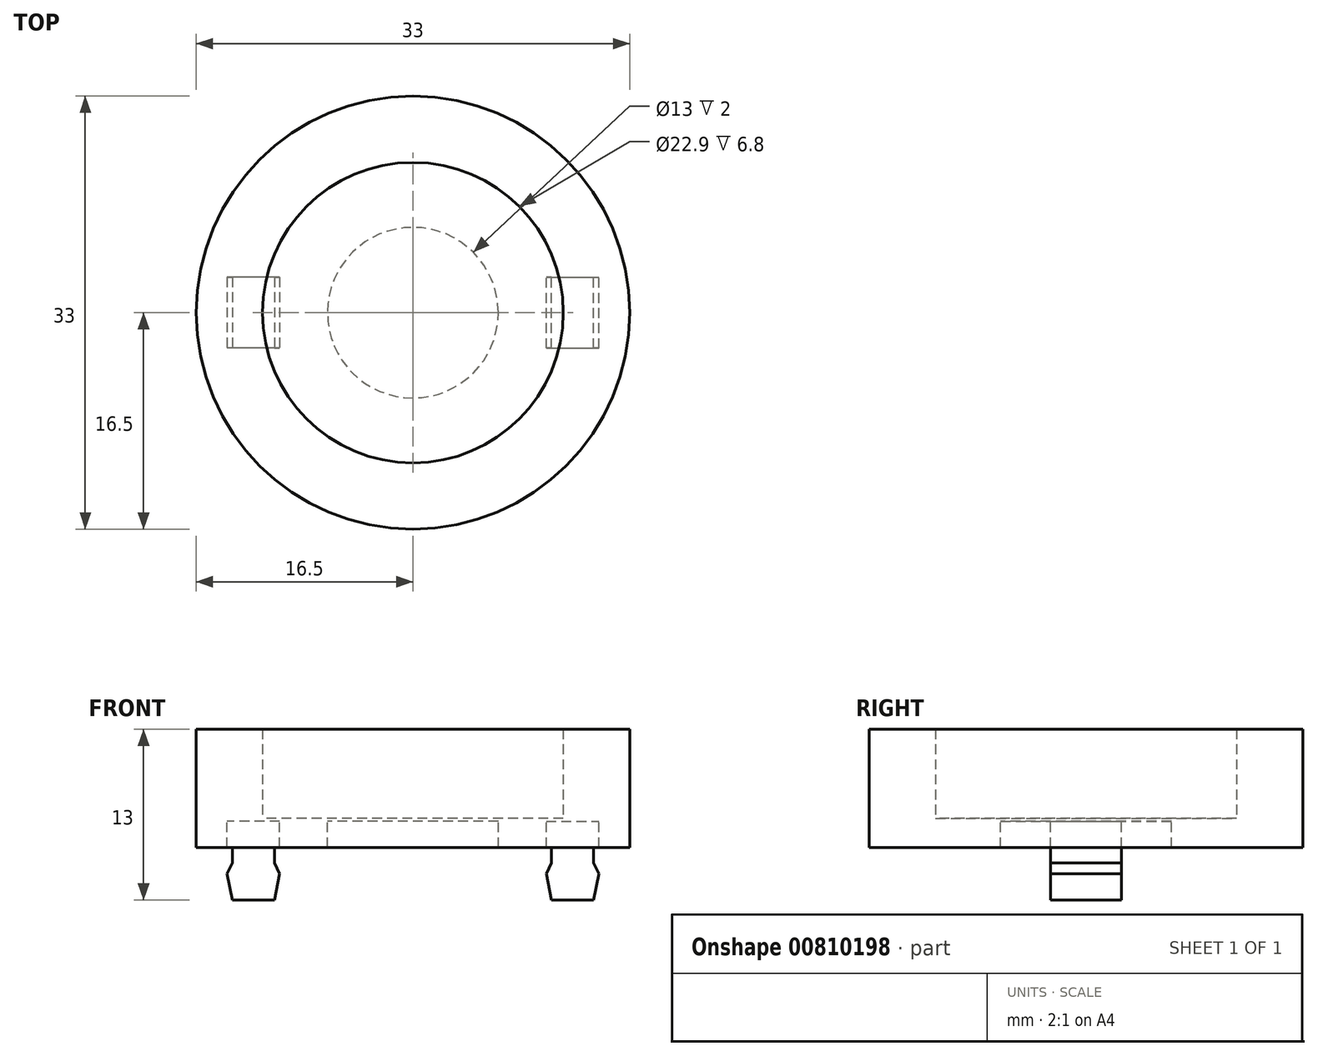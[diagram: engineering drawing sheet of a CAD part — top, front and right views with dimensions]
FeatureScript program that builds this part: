
annotation { "Feature Type Name" : "Feature", "Feature Type Description" : "" }
export const myFeature = defineFeature(function(context is Context, id is Id, definition is map)
    precondition{}
    {
        {
            var Q0;
            Q0=qCreatedBy(makeId("Top.planeOp"),FACE);
            var sketch = newSketch(context, id + "F0", { "sketchPlane" : qUnion([Q0])});
            skCircle(sketch, "E0", {"center": v(0, 0) * mm, "radius": 6.5 * mm});
            skCircle(sketch, "E1", {"center": v(0, 0) * mm, "radius": 16.5 * mm});
            skCircle(sketch, "E2", {"center": v(0, 0) * mm, "radius": 11.45 * mm});
            skLineSegment(sketch, "E3", {"start": v(0, 0) * mm, "end": v(12.15, 0) * mm, "construction": true});
            skLineSegment(sketch, "E4.bottom", {"start": v(10.15, -2.7) * mm, "end": v(14.15, -2.7) * mm});
            skLineSegment(sketch, "E4.top", {"start": v(10.15, 2.7) * mm, "end": v(14.15, 2.7) * mm});
            skLineSegment(sketch, "E4.left", {"start": v(10.15, -2.7) * mm, "end": v(10.15, 2.7) * mm});
            skLineSegment(sketch, "E4.right", {"start": v(14.15, -2.7) * mm, "end": v(14.15, 2.7) * mm});
            skPoint(sketch, "E4.middle", {"position": v(12.15, 0) * mm});
            skSolve(sketch);
        }
        {
            var Q0;
            Q0=makeQuery(id+"F0.imprint","IMPRINT",FACE,{"disambiguationData":[TD([[makeQuery(id+"F0.imprint","IMPRINT",EDGE,{"derivedFrom":sQuery(id+"F0.wireOp",EDGE,"E0")}),-1.0]])]});
            var Q1;
            Q1=makeQuery(id+"F0.imprint","IMPRINT",FACE,{"disambiguationData":[TD([[makeQuery(id+"F0.imprint","IMPRINT",EDGE,{"derivedFrom":sQuery(id+"F0.wireOp",EDGE,"E1")}),1.0]])]});
            var Q2;
            {var subQ5=sQuery(id+"F0.wireOp",EDGE,"E4.left");Q2=makeQuery(id+"F0.imprint","IMPRINT",FACE,{"disambiguationData":[TD([[makeQuery(id+"F0.imprint","IMPRINT",EDGE,{"derivedFrom":subQ5}),-1.0]])]});}
            var Q3;
            {var subQ5=sQuery(id+"F0.wireOp",EDGE,"E4.right");Q3=makeQuery(id+"F0.imprint","IMPRINT",FACE,{"disambiguationData":[TD([[makeQuery(id+"F0.imprint","IMPRINT",EDGE,{"derivedFrom":subQ5}),1.0]])]});}
            extrude(context, id + "F1", {"entities" : qUnion([Q0, Q1, Q2, Q3]), "depth" : 0 * mm, "offsetDistance" : 25 * mm, "hasSecondDirection" : true, "secondDirectionOppositeDirection" : true, "secondDirectionDepth" : 2 * mm});
        }
        {
            var Q0;
            {var subQ5=sQuery(id+"F0.wireOp",EDGE,"E4.right");Q0=makeQuery(id+"F0.imprint","IMPRINT",FACE,{"disambiguationData":[TD([[makeQuery(id+"F0.imprint","IMPRINT",EDGE,{"derivedFrom":subQ5}),1.0]])]});}
            var Q1;
            Q1=makeQuery(id+"F0.imprint","IMPRINT",FACE,{"disambiguationData":[TD([[makeQuery(id+"F0.imprint","IMPRINT",EDGE,{"derivedFrom":sQuery(id+"F0.wireOp",EDGE,"E1")}),1.0]])]});
            extrude(context, id + "F2", {"entities" : qUnion([Q0, Q1]), "operationType" : NewBodyOperationType.ADD, "depth" : 7 * mm, "offsetDistance" : 25 * mm});
        }
        {
            var Q0;
            Q0=makeQuery(id+"F0.imprint","IMPRINT",FACE,{"disambiguationData":[TD([[makeQuery(id+"F0.imprint","IMPRINT",EDGE,{"derivedFrom":sQuery(id+"F0.wireOp",EDGE,"E0")}),-1.0]])]});
            var Q1;
            Q1=makeQuery(id+"F0.imprint","IMPRINT",FACE,{"disambiguationData":[TD([[makeQuery(id+"F0.imprint","IMPRINT",EDGE,{"derivedFrom":sQuery(id+"F0.wireOp",EDGE,"E1")}),1.0]])]});
            var Q2;
            Q2=makeQuery(id+"F0.imprint","IMPRINT",FACE,{"disambiguationData":[TD([[makeQuery(id+"F0.imprint","IMPRINT",EDGE,{"derivedFrom":sQuery(id+"F0.wireOp",EDGE,"E0")}),1.0]])]});
            var Q3;
            {var subQ5=sQuery(id+"F0.wireOp",EDGE,"E4.left");Q3=makeQuery(id+"F0.imprint","IMPRINT",FACE,{"disambiguationData":[TD([[makeQuery(id+"F0.imprint","IMPRINT",EDGE,{"derivedFrom":subQ5}),-1.0]])]});}
            extrude(context, id + "F3", {"entities" : qUnion([Q0, Q1, Q2, Q3]), "operationType" : NewBodyOperationType.ADD, "depth" : 0.2 * mm, "hasOffset" : true, "offsetDistance" : 1.8 * mm});
        }
        {
            var Q0;
            Q0=makeQuery(id+"F0.imprint","IMPRINT",FACE,{"disambiguationData":[TD([[makeQuery(id+"F0.imprint","IMPRINT",EDGE,{"derivedFrom":sQuery(id+"F0.wireOp",EDGE,"E4.bottom")}),1.0]])]});
            extrude(context, id + "F4", {"entities" : qUnion([Q0]), "oppositeDirection" : true, "depth" : 6 * mm, "offsetDistance" : 25 * mm});
        }
        {
            var Q0;
            Q0=makeQuery(id+"F4.opExtrude","SWEPT_FACE",FACE,{"disambiguationData":[OSD([sQuery(id+"F0.wireOp",EDGE,"E4.top")])]});
            var sketch = newSketch(context, id + "F5", { "sketchPlane" : qUnion([Q0])});
            skPoint(sketch, "E5.endSnap0", {"position": v(-12.15, 0) * mm});
            skLineSegment(sketch, "E6", {"start": v(-10.15, -4) * mm, "end": v(-10.55, -3.2) * mm});
            skLineSegment(sketch, "E7", {"start": v(-10.55, -3.2) * mm, "end": v(-10.55, -2) * mm});
            skLineSegment(sketch, "E8", {"start": v(-10.55, -2) * mm, "end": v(-10.15, -2) * mm});
            skLineSegment(sketch, "E9", {"start": v(-10.15, -2) * mm, "end": v(-10.15, -4) * mm});
            skPoint(sketch, "E10", {"position": v(-14.15, -3) * mm});
            skLineSegment(sketch, "E11", {"start": v(-12.15, 0) * mm, "end": v(-12.15, -6) * mm, "construction": true});
            skLineSegment(sketch, "E12.MirrorCS", {"start": v(-14.15, -4) * mm, "end": v(-13.75, -3.2) * mm});
            skLineSegment(sketch, "E13.MirrorCS", {"start": v(-13.75, -3.2) * mm, "end": v(-13.75, -2) * mm});
            skLineSegment(sketch, "E14.MirrorCS", {"start": v(-14.15, -2) * mm, "end": v(-14.15, -4) * mm});
            skLineSegment(sketch, "E15.MirrorCS", {"start": v(-13.75, -2) * mm, "end": v(-14.15, -2) * mm});
            skLineSegment(sketch, "E16", {"start": v(-10.15, -4) * mm, "end": v(-10.55, -6) * mm});
            skLineSegment(sketch, "E17", {"start": v(-10.55, -6) * mm, "end": v(-10.15, -6) * mm});
            skLineSegment(sketch, "E18", {"start": v(-10.15, -6) * mm, "end": v(-10.15, -4) * mm});
            skLineSegment(sketch, "E19.MirrorCS", {"start": v(-14.15, -4) * mm, "end": v(-13.75, -6) * mm});
            skLineSegment(sketch, "E20.MirrorCS", {"start": v(-14.15, -6) * mm, "end": v(-14.15, -4) * mm});
            skLineSegment(sketch, "E21.MirrorCS", {"start": v(-13.75, -6) * mm, "end": v(-14.15, -6) * mm});
            skSolve(sketch);
        }
        {
            var Q0;
            Q0 = qSketchRegion(id + "F5", true);
            extrude(context, id + "F6", {"entities" : qUnion([Q0]), "operationType" : NewBodyOperationType.REMOVE, "oppositeDirection" : true, "depth" : 5.4 * mm, "offsetDistance" : 25 * mm});
        }
        {
            var Q0;
            Q0=qCreatedBy(makeId("Front.planeOp"),FACE);
            var sketch = newSketch(context, id + "F7", { "sketchPlane" : qUnion([Q0])});
            skLineSegment(sketch, "E22", {"start": v(0, 23.02) * mm, "end": v(0, -24.98) * mm, "construction": true});
            skSolve(sketch);
        }
        {
            var Q0;
            Q0=makeQuery(id+"F4.opExtrude","SWEPT_BODY",BODY,{"disambiguationData":[OSD([sQuery(id+"F0.wireOp",EDGE,"E2"),sQuery(id+"F0.wireOp",EDGE,"E4.bottom"),sQuery(id+"F0.wireOp",EDGE,"E4.top"),sQuery(id+"F0.wireOp",EDGE,"E4.left"),sQuery(id+"F0.wireOp",EDGE,"E4.right")])]});
            var Q1;
            Q1=sQuery(id+"F7.wireOp",EDGE,"E22");
            transform(context, id + "F8", {"entities" : qUnion([Q0]), "transformType" : TransformType.ROTATION, "transformAxis" : qUnion([Q1]), "angle" : 180 * degree, "makeCopy" : true});
        }
    });
